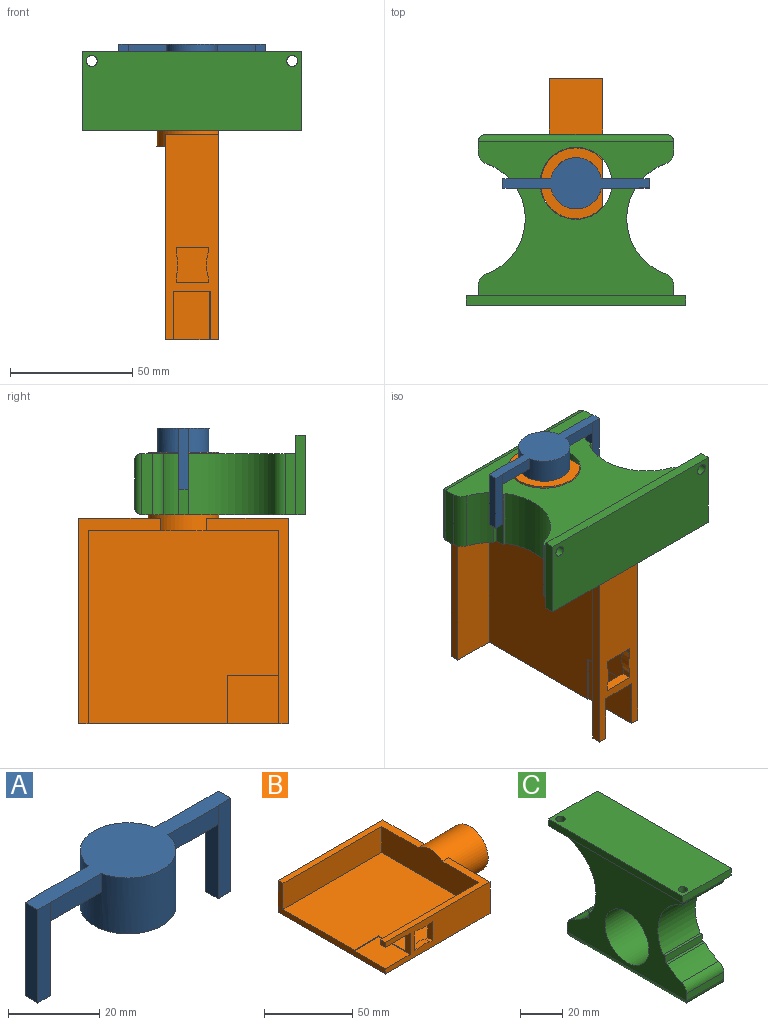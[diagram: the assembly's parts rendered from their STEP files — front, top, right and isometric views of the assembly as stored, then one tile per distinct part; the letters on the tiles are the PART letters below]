
ASSEMBLY  parts=3 mates=1
PART A: 23 faces, bbox 60x21x25 mm
  f0: plane 15.69x5mm, normal (0,1,0), area 78.5mm2, adj f5,f9,f13,f20
  f1: plane 15.69x5mm, normal (0,-1,0), area 78.5mm2, adj f5,f9,f13,f21
  f2: plane 25x3.8mm, normal (1,0,0), area 95mm2, adj f4,f5,f19,f22
  f3: plane 20x3.8mm, normal (-1,0,0), area 76mm2, adj f4,f9,f19,f22
  f4: plane 4x3.8mm, normal (0,0,-1), area 15.2mm2, adj f2,f3,f19,f22
  f5: plane 60x21mm, normal (0,0,1), area 501.7mm2, adj f0,f1,f2,f6,f11,f12,f13,f15
  f6: plane 25x3.9mm, normal (-1,0,0), area 97.5mm2, adj f5,f8,f15,f17
  f7: plane 20x3.9mm, normal (1,0,0), area 78mm2, adj f8,f10,f15,f17
  f8: plane 4x3.9mm, normal (0,0,-1), area 15.6mm2, adj f6,f7,f15,f17
  f9: plane 15.69x4mm, normal (0,0,-1), area 62.3mm2, adj f0,f1,f3,f13,f20,f21
  f10: plane 15.69x4mm, normal (0,0,-1), area 62.3mm2, adj f7,f11,f12,f13,f16,f18
  f11: plane 15.69x5mm, normal (0,-1,0), area 78.5mm2, adj f5,f10,f13,f18
  f12: plane 15.69x5mm, normal (0,1,0), area 78.5mm2, adj f5,f10,f13,f16
  f13: cylinder r=10.5mm len=21mm, axis (0,0,1), area 949.4mm2, adj f0,f1,f5,f9,f10,f11,f12,f14
  f14: plane 21x21mm, normal (0,0,-1), area 346.4mm2, adj f13
  f15: plane 25x4mm, normal (0,1,0), area 100mm2, adj f5,f6,f7,f8,f16
  f16: plane 5x0.05mm, normal (-1,0,0), area 0.3mm2, adj f5,f10,f12,f15
  f17: plane 25x4mm, normal (0,-1,0), area 100mm2, adj f5,f6,f7,f8,f18
  f18: plane 5x0.05mm, normal (-1,0,0), area 0.3mm2, adj f5,f10,f11,f17
  f19: plane 25x4mm, normal (0,1,0), area 100mm2, adj f2,f3,f4,f5,f20
  f20: plane 5x0.1mm, normal (1,0,0), area 0.5mm2, adj f0,f5,f9,f19
  f21: plane 5x0.1mm, normal (1,0,0), area 0.5mm2, adj f1,f5,f9,f22
  f22: plane 25x4mm, normal (0,-1,0), area 100mm2, adj f2,f3,f4,f5,f21
PART B: 29 faces, bbox 111.1x86x25.5 mm
  f0: plane 79.1x18mm, normal (0,1,0), area 952.8mm2, adj f1,f3,f4,f6,f8,f17,f21,f22
  f1: plane 79.1x78mm, normal (0,0,1), area 5749.8mm2, adj f0,f4,f5,f12,f17,f20
  f2: plane 84.1x22mm, normal (0,-1,0), area 1369.2mm2, adj f3,f4,f5,f6,f8,f9,f11,f16
  f3: plane 20x4mm, normal (0,0,-1), area 80mm2, adj f0,f2,f4,f6
  f4: plane 25x15mm, normal (-1,0,0), area 70.5mm2, adj f0,f1,f2,f3,f11,f12
  f5: plane 86x22mm, normal (-1,0,0), area 403.5mm2, adj f1,f2,f7,f9,f10,f11,f12,f20
  f6: plane 4x3.5mm, normal (-1,0,0), area 14mm2, adj f0,f2,f3,f8
  f7: plane 84.1x22mm, normal (0,1,0), area 1850.2mm2, adj f5,f9,f10,f15
  f8: plane 84.1x33.55mm, normal (0,0,1), area 484.2mm2, adj f0,f2,f6,f13,f16,f17
  f9: plane 111.1x86mm, normal (0,0,-1), area 7742.7mm2, adj f2,f5,f7,f13,f14,f15,f16
  f10: plane 84.1x33.55mm, normal (0,0,1), area 484.2mm2, adj f5,f7,f13,f15,f17,f20
  f11: plane 25x20mm, normal (0,0,1), area 500mm2, adj f2,f4,f5,f12
  f12: plane 20x0.5mm, normal (0,-1,0), area 10mm2, adj f1,f4,f5,f11
  f13: cylinder r=14.5mm len=32mm, axis (-1,0,0), area 2007.1mm2, adj f8,f9,f10,f14,f15,f16,f17
  f14: plane 29x25.5mm, normal (1,0,0), area 268.9mm2, adj f9,f13,f18
  f15: plane 33.55x22mm, normal (1,0,0), area 661mm2, adj f7,f9,f10,f13
  f16: plane 33.55x22mm, normal (1,0,0), area 661mm2, adj f2,f8,f9,f13
  f17: plane 78x21.5mm, normal (-1,0,0), area 1449.3mm2, adj f0,f1,f8,f10,f13,f20
  f18: cylinder r=10.5mm len=21mm, axis (1,0,0), area 329.9mm2, adj f14,f19
  f19: plane 21x21mm, normal (1,0,0), area 346.4mm2, adj f18
  f20: plane 79.1x18mm, normal (0,-1,0), area 1423.8mm2, adj f1,f5,f10,f17
  f21: cylinder r=16.62mm len=9.85mm, axis (0,-1,0), area 40mm2, adj f0,f2,f22,f28
  f22: plane 4x2.32mm, normal (0,0,1), area 9.3mm2, adj f0,f2,f21,f23
  f23: plane 13.16x4mm, normal (-1,0,0), area 52.7mm2, adj f0,f2,f22,f24
  f24: plane 4x2.32mm, normal (0,0,-1), area 9.3mm2, adj f0,f2,f23,f25
  f25: cylinder r=16.62mm len=9.85mm, axis (0,-1,0), area 40mm2, adj f0,f2,f24,f26
  f26: plane 4x2.32mm, normal (0,0,-1), area 9.3mm2, adj f0,f2,f25,f27
  f27: plane 13.16x4mm, normal (1,0,0), area 52.7mm2, adj f0,f2,f26,f28
  f28: plane 4x2.32mm, normal (0,0,1), area 9.3mm2, adj f0,f2,f21,f27
PART C: 33 faces, bbox 32.5x90x70 mm
  f0: plane 90x32.5mm, normal (0,0,-1), area 893.2mm2, adj f2,f3,f6,f7,f15,f16,f17,f20
  f1: cylinder r=23.97mm len=35.08mm, axis (-1,0,0), area 1064.8mm2, adj f2,f3,f24,f31
  f2: plane 80x63mm, normal (-1,0,0), area 2991.4mm2, adj f0,f1,f4,f6,f7,f8,f9,f12
  f3: plane 90x67mm, normal (1,0,0), area 3351.4mm2, adj f0,f1,f4,f5,f6,f7,f8,f9
  f4: cylinder r=23.97mm len=35.08mm, axis (-1,0,0), area 1064.8mm2, adj f2,f3,f23,f26
  f5: plane 90x32.5mm, normal (0,0,1), area 2893.2mm2, adj f3,f15,f16,f17,f20,f21
  f6: plane 25x4.21mm, normal (0,1,0), area 105.3mm2, adj f0,f2,f3,f24
  f7: plane 25x4.21mm, normal (0,-1,0), area 105.3mm2, adj f0,f2,f3,f23
  f8: plane 25x4.21mm, normal (0,1,0), area 105.3mm2, adj f2,f3,f11,f25
  f9: plane 25x4.21mm, normal (0,-1,0), area 105.3mm2, adj f2,f3,f14,f22
  f10: plane 74x19mm, normal (0,0,-1), area 1406mm2, adj f11,f12,f13,f14
  f11: cylinder r=3mm len=25mm, axis (-1,0,0), area 107.5mm2, adj f8,f10,f12,f13
  f12: cylinder r=3mm len=80mm, axis (0,-1,0), area 366.7mm2, adj f2,f10,f11,f14
  f13: cylinder r=3mm len=80mm, axis (0,1,0), area 366.7mm2, adj f3,f10,f11,f14
  f14: cylinder r=3mm len=25mm, axis (1,0,0), area 107.5mm2, adj f9,f10,f12,f13
  f15: plane 32.5x4mm, normal (0,1,0), area 130mm2, adj f0,f3,f5,f16
  f16: plane 90x4mm, normal (-1,0,0), area 360mm2, adj f0,f5,f15,f17
  f17: plane 32.5x4mm, normal (0,-1,0), area 130mm2, adj f0,f3,f5,f16
  f18: cylinder r=23.97mm len=25mm, axis (-1,0,0), area 281.1mm2, adj f2,f3,f22,f28
  f19: cylinder r=23.97mm len=25mm, axis (-1,0,0), area 281.1mm2, adj f2,f3,f25,f30
  f20: cylinder r=2.25mm len=4.5mm, axis (0,0,-1), area 56.5mm2, adj f0,f5
  f21: cylinder r=2.25mm len=4.5mm, axis (0,0,-1), area 56.5mm2, adj f0,f5
  f22: cylinder r=5mm len=25mm, axis (-1,0,0), area 153.5mm2, adj f2,f3,f9,f18
  f23: cylinder r=5mm len=25mm, axis (-1,0,0), area 153.5mm2, adj f2,f3,f4,f7
  f24: cylinder r=5mm len=25mm, axis (-1,0,0), area 153.5mm2, adj f1,f2,f3,f6
  f25: cylinder r=5mm len=25mm, axis (-1,0,0), area 153.5mm2, adj f2,f3,f8,f19
  f26: plane 25x1.37mm, normal (0,0,1), area 34.1mm2, adj f2,f3,f4,f27
  f27: plane 25x4mm, normal (0,-1,0), area 100mm2, adj f2,f3,f26,f28
  f28: plane 25x1.7mm, normal (0,0,1), area 42.5mm2, adj f2,f3,f18,f27
  f29: plane 25x4mm, normal (0,1,0), area 100mm2, adj f2,f3,f30,f31
  f30: plane 25x1.7mm, normal (0,0,1), area 42.5mm2, adj f2,f3,f19,f29
  f31: plane 25x1.37mm, normal (0,0,1), area 34.1mm2, adj f1,f2,f3,f29
  f32: cylinder r=14.75mm len=29.5mm, axis (1,0,0), area 2316.9mm2, adj f2,f3
PLACE A t=(30.24,38.92,50.68)mm
PLACE B rot(axis=(0,-1,0),90deg) t=(41.24,38.92,-65.42)mm
PLACE C rot(axis=(0.58,0.58,-0.58),120deg) t=(9.57,58.92,-7.55)mm
MATE fastened B.f13 <-> A.f13  axis (0,0,1) through (30.24,38.92,40.68)mm
